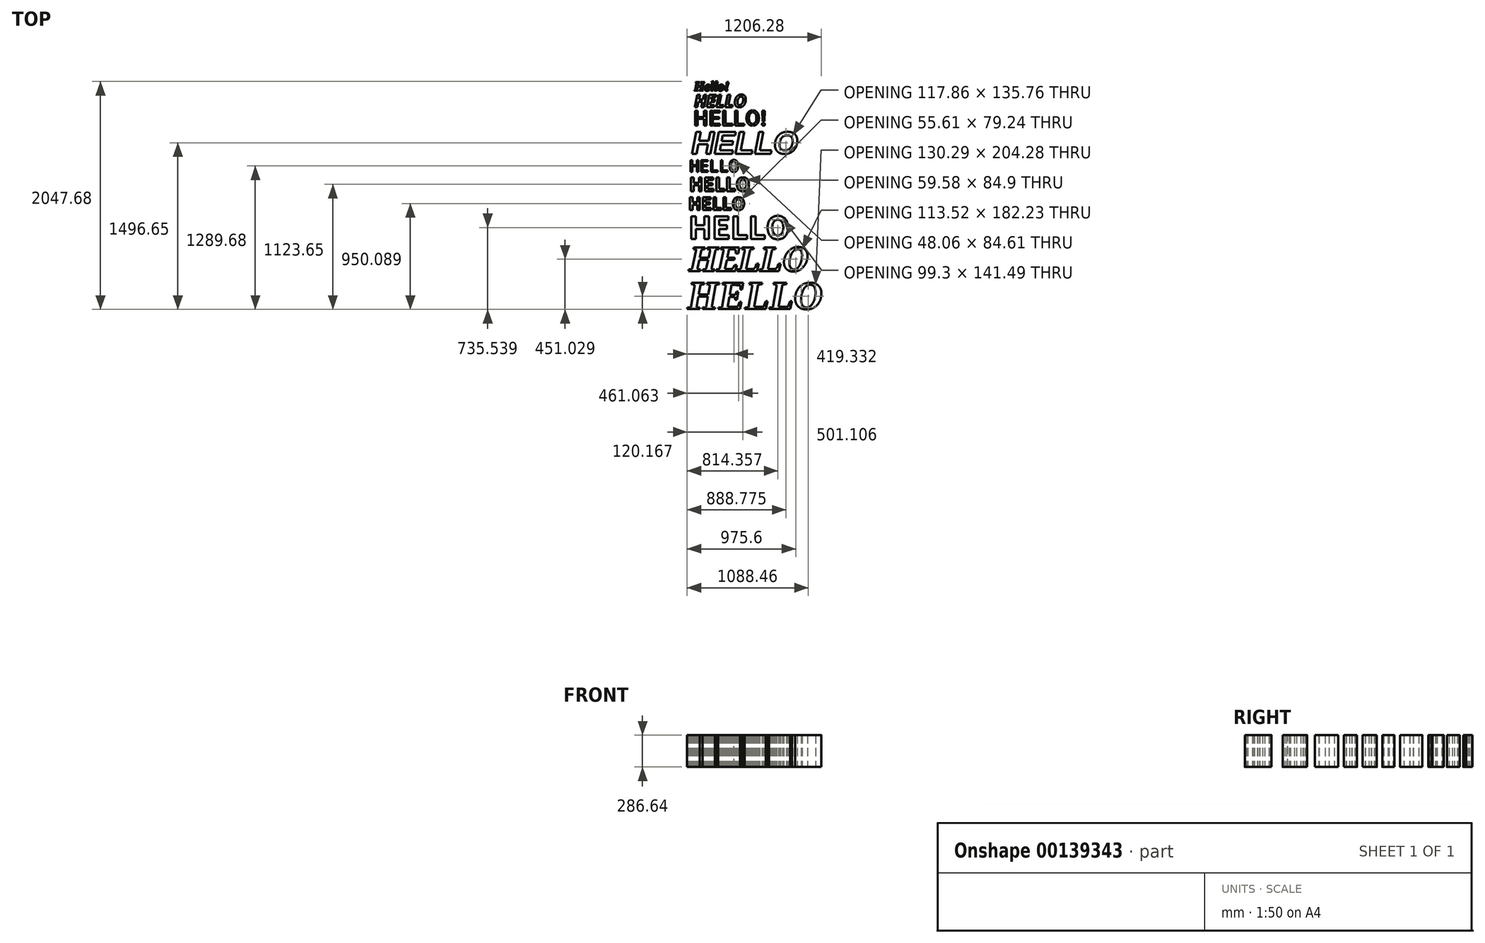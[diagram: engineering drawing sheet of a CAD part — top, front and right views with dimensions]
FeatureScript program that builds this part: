
annotation { "Feature Type Name" : "Feature", "Feature Type Description" : "" }
export const myFeature = defineFeature(function(context is Context, id is Id, definition is map)
    precondition{}
    {
        {
            var Q0;
            Q0=qCreatedBy(makeId("Top.planeOp"),FACE);
            var sketch = newSketch(context, id + "F0", { "sketchPlane" : qUnion([Q0])});
            skText(sketch, "E0", { "text": "Hello!", "fontName": "Tinos-BoldItalic.ttf"});
            skText(sketch, "E1", { "text": "HELLO", "fontName": "OpenSans-BoldItalic.ttf"});
            skText(sketch, "E2", { "text": "HELLO!", "fontName": "AllertaStencil-Regular.ttf"});
            skText(sketch, "E3", { "text": "HELLO", "fontName": "Arimo-BoldItalic.ttf"});
            skText(sketch, "E4", { "text": "HELLO", "fontName": "DroidSansMono.ttf"});
            skText(sketch, "E5", { "text": "HELLO", "fontName": "NotoSansCJKsc-Bold.otf"});
            skText(sketch, "E6", { "text": "HELLO", "fontName": "NotoSansCJKtc-Bold.otf"});
            skText(sketch, "E7", { "text": "HELLO", "fontName": "NotoSansCJKjp-Bold.otf"});
            skText(sketch, "E8", { "text": "HELLO", "fontName": "NotoSerif-BoldItalic.ttf"});
            skText(sketch, "E9", { "text": "HELLO", "fontName": "Tinos-BoldItalic.ttf"});
            const initialGuessF0  = {"E0": [-0.12725, -0.04043, 1, 0, 0.08572], "E1": [-0.12592, -0.18734, 1, 0, 0.11206], "E2": [-0.13528, -0.35375, 1, 0, 0.13452], "E3": [-0.15195, -0.60598, 1, 0, 0.20325], "E4": [-0.1677, -0.7684, 1, 0, 0.10592], "E5": [-0.17034, -0.94317, 1, 0, 0.11916], "E6": [-0.17828, -1.11265, 1, 0, 0.11122], "E7": [-0.17828, -1.37217, 1, 0, 0.1986], "E8": [-0.17002, -1.6622, 1, 0, 0.21687], "E9": [-0.18703, -2.00197, 1, 0, 0.2579]};
            skSetInitialGuess(sketch, initialGuessF0);
            skSolve(sketch);
        }
        {
            var Q0;
            Q0 = qSketchRegion(id + "F0", true);
            extrude(context, id + "F1", {"entities" : qUnion([Q0]), "depth" : 286.64 * mm});
        }
    });
